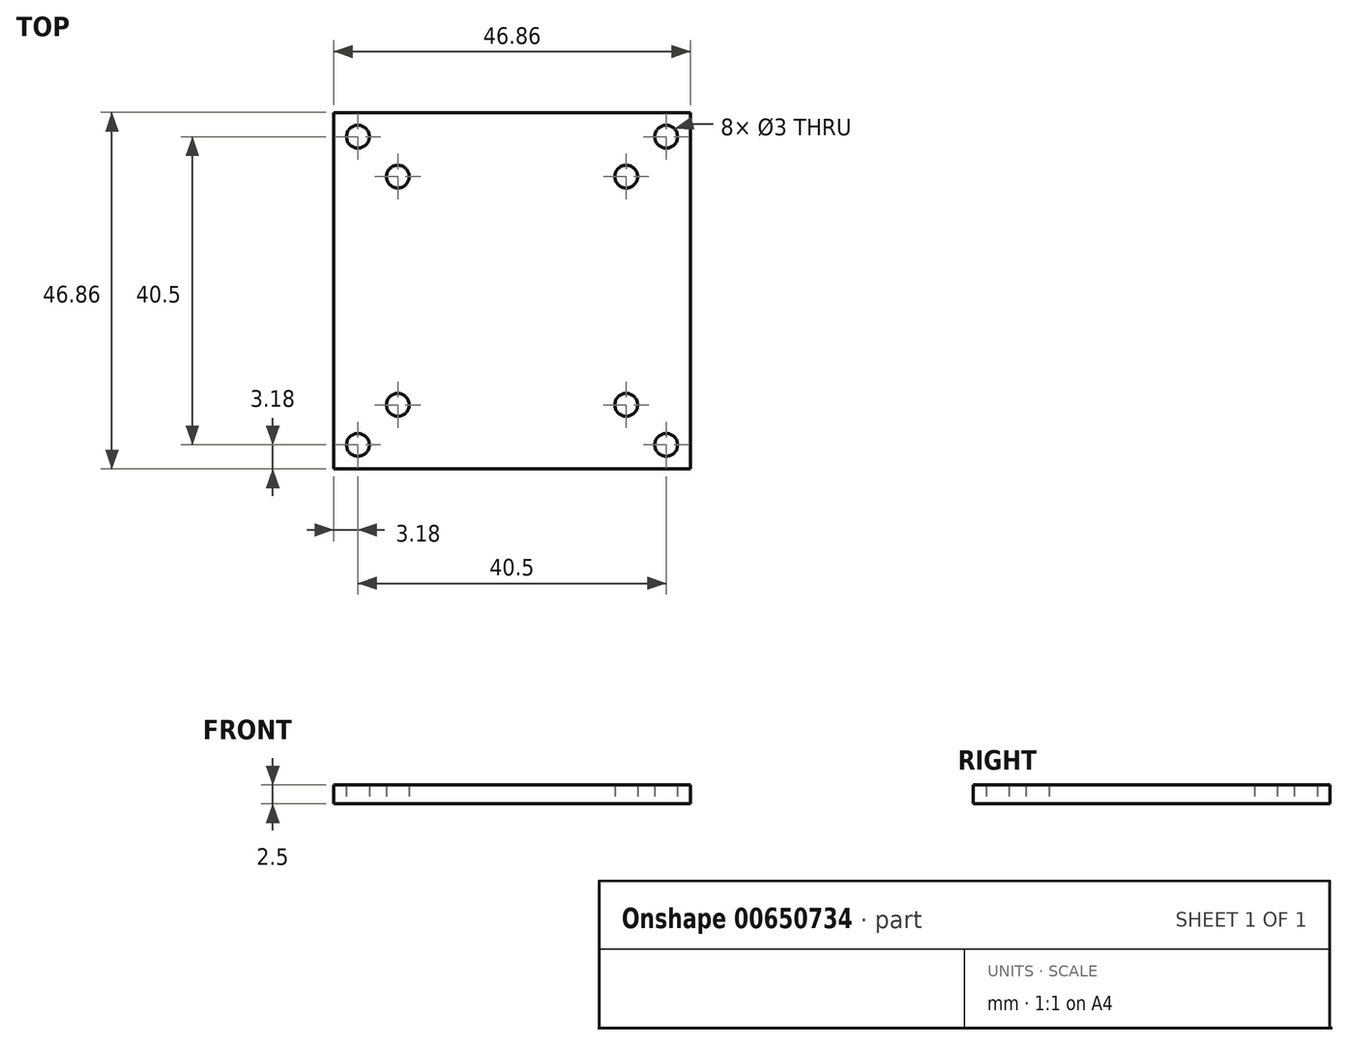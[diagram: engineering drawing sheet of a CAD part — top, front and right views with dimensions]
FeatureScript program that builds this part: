
annotation { "Feature Type Name" : "Feature", "Feature Type Description" : "" }
export const myFeature = defineFeature(function(context is Context, id is Id, definition is map)
    precondition{}
    {
        {
            var Q0;
            Q0=qCreatedBy(makeId("Top.planeOp"),FACE);
            var sketch = newSketch(context, id + "F0", { "sketchPlane" : qUnion([Q0])});
            skCircle(sketch, "E0", {"center": v(20.25, 20.25) * mm, "radius": 1.5 * mm});
            skCircle(sketch, "E1.MirrorC", {"center": v(-20.25, 20.25) * mm, "radius": 1.5 * mm});
            skCircle(sketch, "E2.MirrorC", {"center": v(-20.25, -20.25) * mm, "radius": 1.5 * mm});
            skCircle(sketch, "E3.MirrorC", {"center": v(20.25, -20.25) * mm, "radius": 1.5 * mm});
            skLineSegment(sketch, "E4.bottom", {"start": v(-23.42, 23.42) * mm, "end": v(23.42, 23.42) * mm});
            skLineSegment(sketch, "E4.top", {"start": v(-23.42, -23.42) * mm, "end": v(23.42, -23.42) * mm});
            skLineSegment(sketch, "E4.left", {"start": v(-23.42, 23.42) * mm, "end": v(-23.42, -23.42) * mm});
            skLineSegment(sketch, "E4.right", {"start": v(23.42, 23.42) * mm, "end": v(23.42, -23.42) * mm});
            skCircle(sketch, "E5", {"center": v(15, 15) * mm, "radius": 1.5 * mm});
            skCircle(sketch, "E6.MirrorC", {"center": v(-15, 15) * mm, "radius": 1.5 * mm});
            skCircle(sketch, "E7.MirrorC", {"center": v(-15, -15) * mm, "radius": 1.5 * mm});
            skCircle(sketch, "E8.MirrorC", {"center": v(15, -15) * mm, "radius": 1.5 * mm});
            skLineSegment(sketch, "E9.bottom", {"start": v(-15, 17) * mm, "end": v(15, 17) * mm, "construction": true});
            skLineSegment(sketch, "E9.top", {"start": v(-15, -17) * mm, "end": v(15, -17) * mm, "construction": true});
            skLineSegment(sketch, "E9.left", {"start": v(-17, 15) * mm, "end": v(-17, -15) * mm, "construction": true});
            skLineSegment(sketch, "E9.right", {"start": v(17, 15) * mm, "end": v(17, -15) * mm, "construction": true});
            skPoint(sketch, "E10.visualSharp", {"position": v(-17, 17) * mm});
            skArc(sketch, "E10.filletArc", {"start": v(-15, 17) * mm, "mid": v(-16.41, 16.41) * mm, "end": v(-17, 15) * mm, "construction": true});
            skPoint(sketch, "E11.visualSharp", {"position": v(17, 17) * mm});
            skArc(sketch, "E11.filletArc", {"start": v(17, 15) * mm, "mid": v(16.41, 16.41) * mm, "end": v(15, 17) * mm, "construction": true});
            skPoint(sketch, "E12.visualSharp", {"position": v(17, -17) * mm});
            skArc(sketch, "E12.filletArc", {"start": v(15, -17) * mm, "mid": v(16.41, -16.41) * mm, "end": v(17, -15) * mm, "construction": true});
            skPoint(sketch, "E13.visualSharp", {"position": v(-17, -17) * mm});
            skArc(sketch, "E13.filletArc", {"start": v(-17, -15) * mm, "mid": v(-16.41, -16.41) * mm, "end": v(-15, -17) * mm, "construction": true});
            skCircle(sketch, "E14", {"center": v(-20.25, 20.25) * mm, "radius": 3.18 * mm, "construction": true});
            skSolve(sketch);
        }
        {
            var Q0;
            Q0 = qSketchRegion(id + "F0", true);
            extrude(context, id + "F1", {"entities" : qUnion([Q0]), "depth" : 2.5 * mm, "offsetDistance" : 25.4 * mm});
        }
    });
